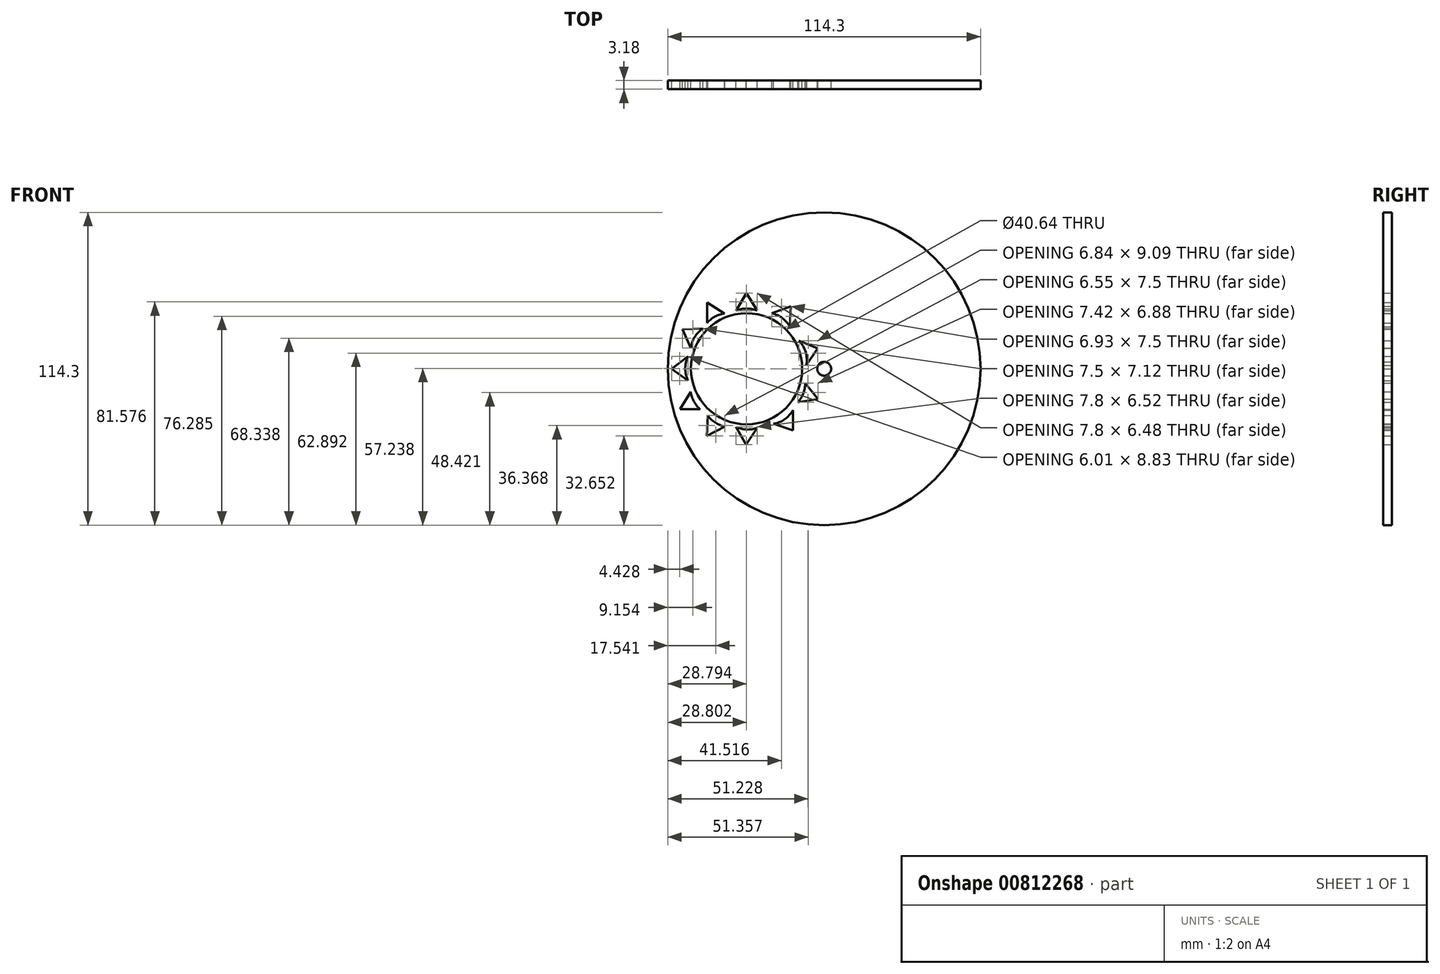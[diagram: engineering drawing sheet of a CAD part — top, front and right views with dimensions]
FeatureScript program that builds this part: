
annotation { "Feature Type Name" : "Feature", "Feature Type Description" : "" }
export const myFeature = defineFeature(function(context is Context, id is Id, definition is map)
    precondition{}
    {
        {
            var Q0;
            Q0=qCreatedBy(makeId("Front.planeOp"),FACE);
            var sketch = newSketch(context, id + "F0", { "sketchPlane" : qUnion([Q0])});
            skCircle(sketch, "E0", {"center": v(0, 0) * mm, "radius": 57.15 * mm});
            skCircle(sketch, "E1", {"center": v(0, 0) * mm, "radius": 2.54 * mm});
            skCircle(sketch, "E2", {"center": v(-28.35, 0) * mm, "radius": 20.32 * mm});
            skArc(sketch, "E3", {"start": v(-49.72, 4.5) * mm, "mid": v(-50.73, 0.09) * mm, "end": v(-49.72, -4.33) * mm});
            skLineSegment(sketch, "E4", {"start": v(-49.72, -4.33) * mm, "end": v(-55.72, 0) * mm});
            skLineSegment(sketch, "E5", {"start": v(-55.72, 0) * mm, "end": v(-49.72, 4.5) * mm});
            skArc(sketch, "E6", {"start": v(-24.46, 21.25) * mm, "mid": v(-28.36, 22) * mm, "end": v(-32.26, 21.19) * mm});
            skLineSegment(sketch, "E7", {"start": v(-32.26, 21.19) * mm, "end": v(-28.36, 27.66) * mm});
            skPoint(sketch, "E7.endSnap0", {"position": v(-28.36, 22) * mm});
            skLineSegment(sketch, "E8", {"start": v(-28.36, 27.66) * mm, "end": v(-24.46, 21.25) * mm});
            skArc(sketch, "E9", {"start": v(-32.26, -21.24) * mm, "mid": v(-28.4, -22.19) * mm, "end": v(-24.46, -21.58) * mm});
            skLineSegment(sketch, "E10", {"start": v(-32.26, -21.24) * mm, "end": v(-28.54, -27.76) * mm});
            skLineSegment(sketch, "E11", {"start": v(-28.54, -27.76) * mm, "end": v(-24.46, -21.58) * mm});
            skArc(sketch, "E12", {"start": v(-36.36, 20.21) * mm, "mid": v(-39.87, 19.08) * mm, "end": v(-42.74, 16.76) * mm});
            skArc(sketch, "E13", {"start": v(-44.25, 14.75) * mm, "mid": v(-47.25, 11.67) * mm, "end": v(-48.72, 7.63) * mm});
            skArc(sketch, "E14", {"start": v(-48.74, -8.4) * mm, "mid": v(-47.59, -11.93) * mm, "end": v(-45.26, -14.8) * mm});
            skArc(sketch, "E15", {"start": v(-42.54, -17.03) * mm, "mid": v(-39.82, -19.64) * mm, "end": v(-36.33, -21.08) * mm});
            skArc(sketch, "E16", {"start": v(-12.55, 15.39) * mm, "mid": v(-15.31, 18.53) * mm, "end": v(-19.1, 20.3) * mm});
            skArc(sketch, "E17", {"start": v(-9.63, -12.17) * mm, "mid": v(-7.61, -8.99) * mm, "end": v(-6.9, -5.29) * mm});
            skArc(sketch, "E18", {"start": v(-18.5, -20.13) * mm, "mid": v(-14.4, -18.45) * mm, "end": v(-11.4, -15.17) * mm});
            skLineSegment(sketch, "E19", {"start": v(-48.72, 7.63) * mm, "end": v(-51.75, 14.38) * mm});
            skLineSegment(sketch, "E20", {"start": v(-51.75, 14.38) * mm, "end": v(-44.25, 14.75) * mm});
            skLineSegment(sketch, "E21", {"start": v(-42.74, 16.76) * mm, "end": v(-42.74, 24.17) * mm});
            skLineSegment(sketch, "E22", {"start": v(-42.74, 24.17) * mm, "end": v(-36.36, 20.21) * mm});
            skLineSegment(sketch, "E23", {"start": v(-19.1, 20.3) * mm, "end": v(-12.17, 22.88) * mm});
            skLineSegment(sketch, "E24", {"start": v(-12.17, 22.88) * mm, "end": v(-12.55, 15.39) * mm});
            skLineSegment(sketch, "E25", {"start": v(-6.9, -5.29) * mm, "end": v(-2.21, -11.02) * mm});
            skLineSegment(sketch, "E26", {"start": v(-2.21, -11.02) * mm, "end": v(-9.63, -12.17) * mm});
            skLineSegment(sketch, "E27", {"start": v(-11.4, -15.17) * mm, "end": v(-11.4, -22.58) * mm});
            skLineSegment(sketch, "E28", {"start": v(-11.4, -22.58) * mm, "end": v(-18.5, -20.13) * mm});
            skLineSegment(sketch, "E29", {"start": v(-36.33, -21.08) * mm, "end": v(-42.88, -24.53) * mm});
            skLineSegment(sketch, "E30", {"start": v(-42.88, -24.53) * mm, "end": v(-42.54, -17.03) * mm});
            skLineSegment(sketch, "E31", {"start": v(-45.26, -14.8) * mm, "end": v(-52.66, -14.8) * mm});
            skLineSegment(sketch, "E32", {"start": v(-52.66, -14.8) * mm, "end": v(-48.74, -8.4) * mm});
            skArc(sketch, "E33", {"start": v(-6.51, 1.2) * mm, "mid": v(-6.74, 6.08) * mm, "end": v(-9.21, 10.29) * mm});
            skLineSegment(sketch, "E34", {"start": v(-9.21, 10.29) * mm, "end": v(-2.37, 7.46) * mm});
            skLineSegment(sketch, "E35", {"start": v(-2.37, 7.46) * mm, "end": v(-6.51, 1.2) * mm});
            skSolve(sketch);
        }
        {
            var Q0;
            Q0=makeQuery(id+"F0.imprint","IMPRINT",FACE,{"disambiguationData":[TD([[makeQuery(id+"F0.imprint","IMPRINT",EDGE,{"derivedFrom":sQuery(id+"F0.wireOp",EDGE,"E0")}),1.0]])]});
            extrude(context, id + "F1", {"entities" : qUnion([Q0]), "depth" : 3.17 * mm, "offsetDistance" : 25.4 * mm});
        }
    });
